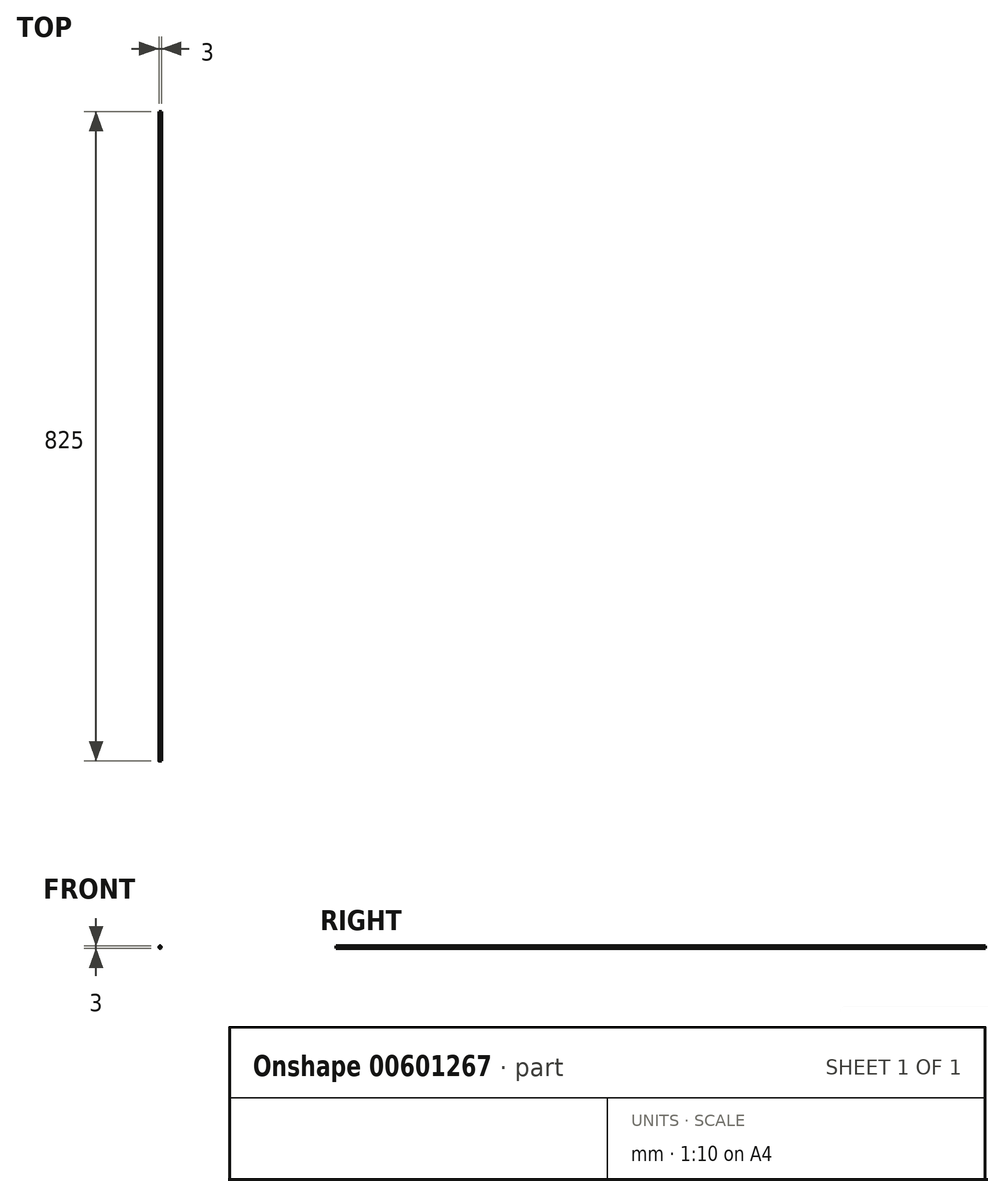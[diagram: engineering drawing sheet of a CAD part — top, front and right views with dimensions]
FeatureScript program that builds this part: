
annotation { "Feature Type Name" : "Feature", "Feature Type Description" : "" }
export const myFeature = defineFeature(function(context is Context, id is Id, definition is map)
    precondition{}
    {
        {
            var Q0;
            Q0=qCreatedBy(makeId("Front.planeOp"),FACE);
            var sketch = newSketch(context, id + "F0", { "sketchPlane" : qUnion([Q0])});
            skCircle(sketch, "E0", {"center": v(0, 0) * mm, "radius": 1.5 * mm});
            skSolve(sketch);
        }
        {
            var Q0;
            Q0=makeQuery(id+"F0.imprint","IMPRINT",FACE,{"disambiguationData":[TD([[makeQuery(id+"F0.imprint","IMPRINT",EDGE,{"derivedFrom":sQuery(id+"F0.wireOp",EDGE,"E0")}),1.0]])]});
            extrude(context, id + "F1", {"entities" : qUnion([Q0]), "depth" : 825 * mm, "offsetDistance" : 25 * mm});
        }
    });
